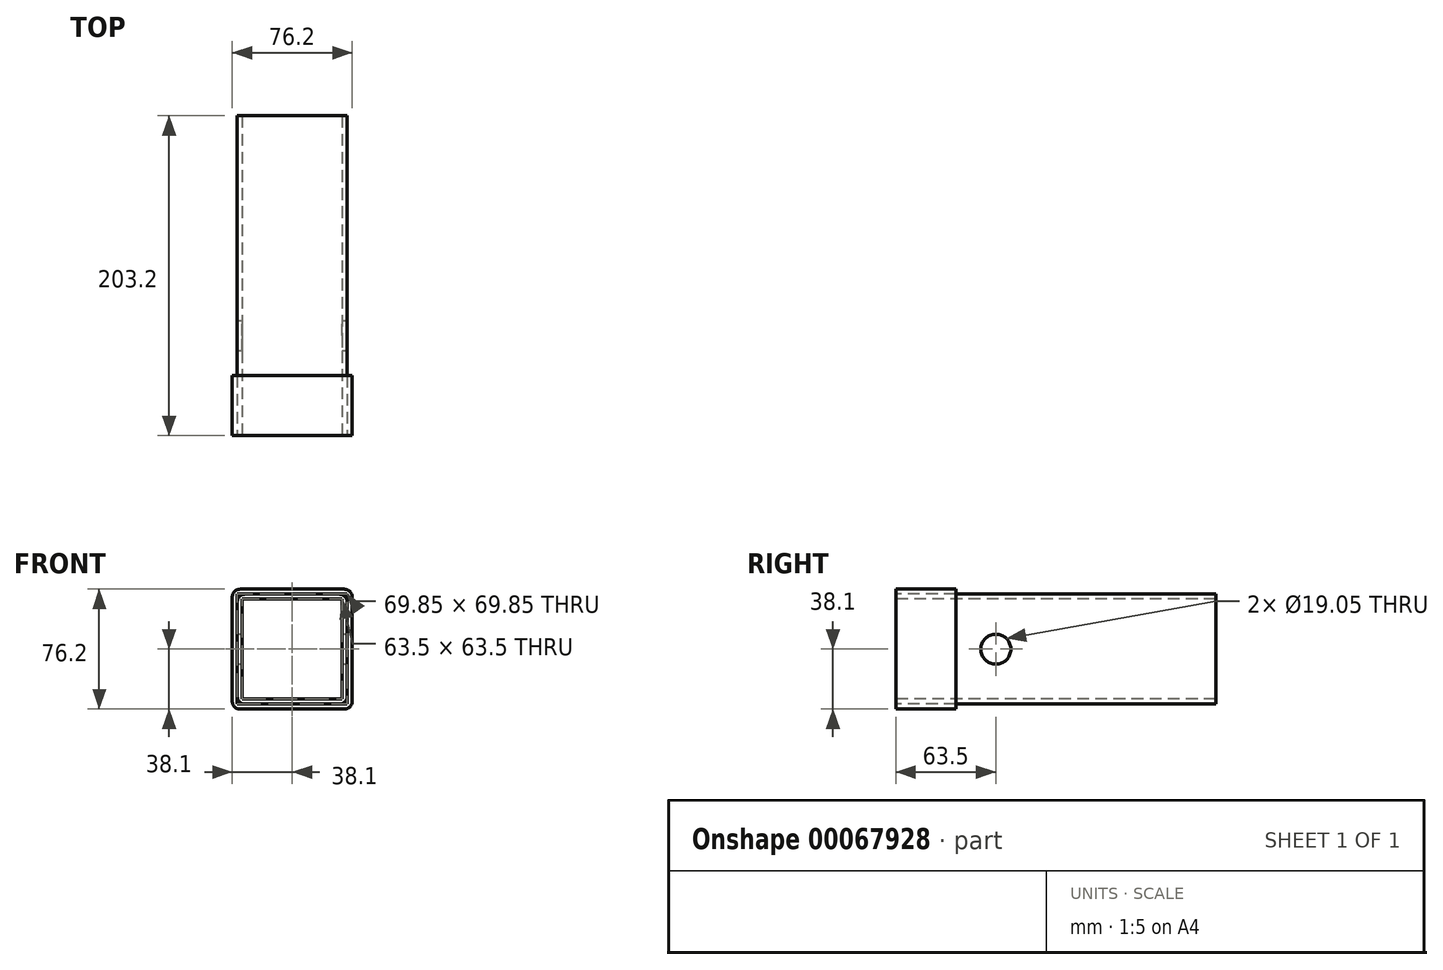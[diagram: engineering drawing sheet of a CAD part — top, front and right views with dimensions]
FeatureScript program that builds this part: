
annotation { "Feature Type Name" : "Feature", "Feature Type Description" : "" }
export const myFeature = defineFeature(function(context is Context, id is Id, definition is map)
    precondition{}
    {
        {
            var Q0;
            Q0=qCreatedBy(makeId("Front.planeOp"),FACE);
            var sketch = newSketch(context, id + "F0", { "sketchPlane" : qUnion([Q0])});
            skLineSegment(sketch, "E0.rect.bottom", {"start": v(31.75, 31.75) * mm, "end": v(-31.75, 31.75) * mm});
            skLineSegment(sketch, "E0.rect.top", {"start": v(31.75, -31.75) * mm, "end": v(-31.75, -31.75) * mm});
            skLineSegment(sketch, "E0.rect.left", {"start": v(31.75, 31.75) * mm, "end": v(31.75, -31.75) * mm});
            skLineSegment(sketch, "E0.rect.right", {"start": v(-31.75, 31.75) * mm, "end": v(-31.75, -31.75) * mm});
            skPoint(sketch, "E0.rect.middle", {"position": v(0, 0) * mm});
            skLineSegment(sketch, "E1.rect.bottom", {"start": v(34.93, 34.93) * mm, "end": v(-34.93, 34.92) * mm});
            skLineSegment(sketch, "E1.rect.top", {"start": v(34.93, -34.92) * mm, "end": v(-34.93, -34.93) * mm});
            skLineSegment(sketch, "E1.rect.left", {"start": v(34.93, 34.93) * mm, "end": v(34.93, -34.92) * mm});
            skLineSegment(sketch, "E1.rect.right", {"start": v(-34.93, 34.92) * mm, "end": v(-34.93, -34.93) * mm});
            skLineSegment(sketch, "E2.rect.bottom", {"start": v(38.1, 38.1) * mm, "end": v(-38.1, 38.1) * mm});
            skLineSegment(sketch, "E2.rect.top", {"start": v(38.1, -38.1) * mm, "end": v(-38.1, -38.1) * mm});
            skLineSegment(sketch, "E2.rect.left", {"start": v(38.1, 38.1) * mm, "end": v(38.1, -38.1) * mm});
            skLineSegment(sketch, "E2.rect.right", {"start": v(-38.1, 38.1) * mm, "end": v(-38.1, -38.1) * mm});
            skSolve(sketch);
        }
        {
            var Q0;
            Q0=makeQuery(id+"F0.imprint","IMPRINT",FACE,{"disambiguationData":[TD([[makeQuery(id+"F0.imprint","IMPRINT",EDGE,{"derivedFrom":sQuery(id+"F0.wireOp",EDGE,"E0.rect.bottom")}),-1.0]])]});
            extrude(context, id + "F1", {"entities" : qUnion([Q0]), "oppositeDirection" : true, "depth" : 203.2 * mm});
        }
        {
            var Q0;
            Q0 = qSketchRegion(id + "F0", true);
            extrude(context, id + "F2", {"entities" : qUnion([Q0]), "oppositeDirection" : true, "depth" : 38.1 * mm});
        }
        {
            var Q0;
            Q0=makeQuery(id+"F1.opExtrude","SWEPT_EDGE",EDGE,{"disambiguationData":[OSD([sQuery(id+"F0.wireOp",EDGE,"E1.rect.bottom"),sQuery(id+"F0.wireOp",EDGE,"E1.rect.left")])]});
            var Q1;
            Q1=makeQuery(id+"F2.opExtrude","SWEPT_EDGE",EDGE,{"disambiguationData":[OSD([sQuery(id+"F0.wireOp",EDGE,"E2.rect.bottom"),sQuery(id+"F0.wireOp",EDGE,"E2.rect.left")])]});
            var Q2;
            Q2=makeQuery(id+"F2.opExtrude","SWEPT_EDGE",EDGE,{"disambiguationData":[OSD([sQuery(id+"F0.wireOp",EDGE,"E2.rect.bottom"),sQuery(id+"F0.wireOp",EDGE,"E2.rect.right")])]});
            var Q3;
            Q3=makeQuery(id+"F1.opExtrude","SWEPT_EDGE",EDGE,{"disambiguationData":[OSD([sQuery(id+"F0.wireOp",EDGE,"E1.rect.bottom"),sQuery(id+"F0.wireOp",EDGE,"E1.rect.right")])]});
            var Q4;
            Q4=makeQuery(id+"F1.opExtrude","SWEPT_EDGE",EDGE,{"disambiguationData":[OSD([sQuery(id+"F0.wireOp",EDGE,"E1.rect.top"),sQuery(id+"F0.wireOp",EDGE,"E1.rect.left")])]});
            var Q5;
            Q5=makeQuery(id+"F2.opExtrude","SWEPT_EDGE",EDGE,{"disambiguationData":[OSD([sQuery(id+"F0.wireOp",EDGE,"E2.rect.top"),sQuery(id+"F0.wireOp",EDGE,"E2.rect.left")])]});
            var Q6;
            Q6=makeQuery(id+"F2.opExtrude","SWEPT_EDGE",EDGE,{"disambiguationData":[OSD([sQuery(id+"F0.wireOp",EDGE,"E2.rect.top"),sQuery(id+"F0.wireOp",EDGE,"E2.rect.right")])]});
            var Q7;
            Q7=makeQuery(id+"F1.opExtrude","SWEPT_EDGE",EDGE,{"disambiguationData":[OSD([sQuery(id+"F0.wireOp",EDGE,"E1.rect.top"),sQuery(id+"F0.wireOp",EDGE,"E1.rect.right")])]});
            fillet(context, id + "F3", {"entities" : qUnion([Q0, Q1, Q2, Q3, Q4, Q5, Q6, Q7]), "radius" : 5.08 * mm, "tangentPropagation" : true, "allowEdgeOverflow" : false});
        }
        {
            var Q0;
            Q0=makeQuery(id+"F1.opExtrude","SWEPT_FACE",FACE,{"disambiguationData":[OSD([sQuery(id+"F0.wireOp",EDGE,"E1.rect.left")])]});
            var sketch = newSketch(context, id + "F4", { "sketchPlane" : qUnion([Q0])});
            skLineSegment(sketch, "E3.0.0", {"start": v(203.2, -29.85) * mm, "end": v(203.2, 29.85) * mm});
            skLineSegment(sketch, "E3.0.1", {"start": v(203.2, 29.85) * mm, "end": v(0, 29.85) * mm});
            skLineSegment(sketch, "E3.0.2", {"start": v(0, 29.85) * mm, "end": v(0, -29.85) * mm});
            skLineSegment(sketch, "E3.0.3", {"start": v(0, -29.85) * mm, "end": v(203.2, -29.85) * mm});
            skCircle(sketch, "E4", {"center": v(63.5, 0) * mm, "radius": 9.53 * mm});
            skSolve(sketch);
        }
        {
            var Q0;
            Q0=sQuery(id+"F4.wireOp",VERTEX,"E4.center");
            var Q1;
            Q1=makeQuery(id+"F1.opExtrude","SWEPT_BODY",BODY,{"disambiguationData":[OSD([sQuery(id+"F0.wireOp",EDGE,"E0.rect.bottom"),sQuery(id+"F0.wireOp",EDGE,"E0.rect.top"),sQuery(id+"F0.wireOp",EDGE,"E0.rect.left"),sQuery(id+"F0.wireOp",EDGE,"E0.rect.right"),sQuery(id+"F0.wireOp",EDGE,"E1.rect.bottom"),sQuery(id+"F0.wireOp",EDGE,"E1.rect.top"),sQuery(id+"F0.wireOp",EDGE,"E1.rect.left"),sQuery(id+"F0.wireOp",EDGE,"E1.rect.right")])]});
            hole(context, id + "F5", {"style" : HoleStyle.SIMPLE, "holeDiameter" : 19.05 * mm, "endStyle" : HoleEndStyle.THROUGH, "locations" : qUnion([Q0]), "scope" : qUnion([Q1])});
        }
    });
